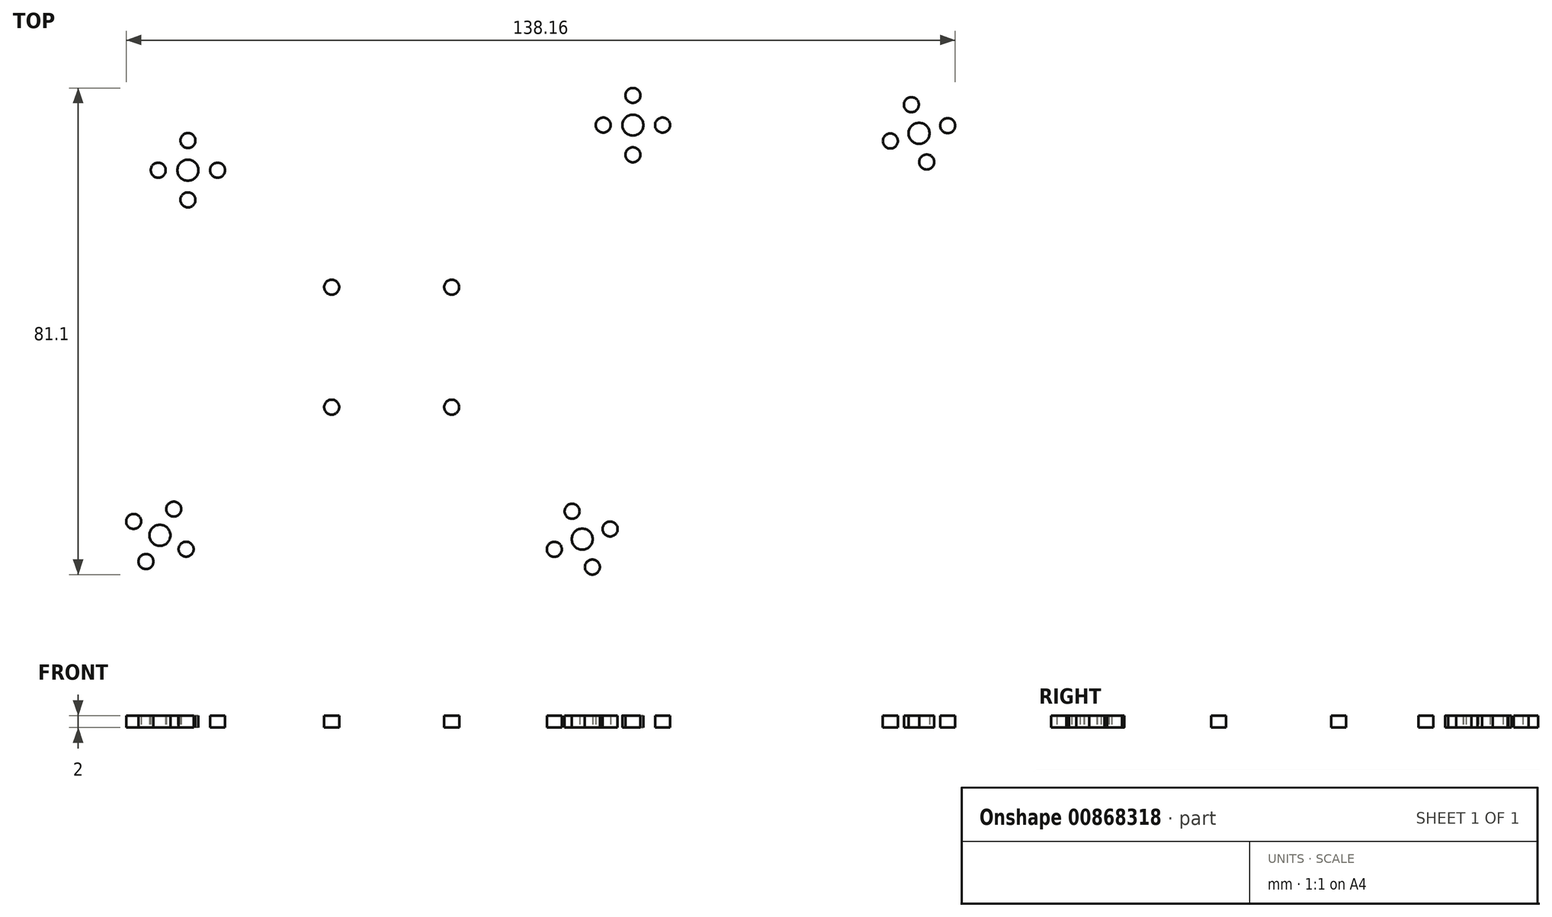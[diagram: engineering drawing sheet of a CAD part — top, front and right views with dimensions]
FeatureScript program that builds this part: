
annotation { "Feature Type Name" : "Feature", "Feature Type Description" : "" }
export const myFeature = defineFeature(function(context is Context, id is Id, definition is map)
    precondition{}
    {
        {
            var Q0;
            Q0=qCreatedBy(makeId("Top.planeOp"),FACE);
            var sketch = newSketch(context, id + "F0", { "sketchPlane" : qUnion([Q0])});
            skLineSegment(sketch, "E0.bottom", {"start": v(10, -2) * mm, "end": v(-10, -2) * mm, "construction": true});
            skLineSegment(sketch, "E0.top", {"start": v(10, 18) * mm, "end": v(-10, 18) * mm, "construction": true});
            skLineSegment(sketch, "E0.left", {"start": v(10, -2) * mm, "end": v(10, 18) * mm, "construction": true});
            skLineSegment(sketch, "E0.right", {"start": v(-10, -2) * mm, "end": v(-10, 0.75) * mm, "construction": true});
            skCircle(sketch, "E1", {"center": v(-10, 18) * mm, "radius": 1.25 * mm});
            skCircle(sketch, "E2.MirrorC", {"center": v(10, 18) * mm, "radius": 1.25 * mm});
            skCircle(sketch, "E3.MirrorC", {"center": v(-10, -2) * mm, "radius": 1.25 * mm});
            skCircle(sketch, "E4.MirrorC", {"center": v(10, -2) * mm, "radius": 1.25 * mm});
            skLineSegment(sketch, "E5", {"start": v(-11.33, 27.1) * mm, "end": v(-11.33, 27.79) * mm});
            skLineSegment(sketch, "E6", {"start": v(-9.22, 27.79) * mm, "end": v(-5.37, 27.79) * mm});
            skLineSegment(sketch, "E7.MirrorCS", {"start": v(9.22, 27.79) * mm, "end": v(5.37, 27.79) * mm});
            skLineSegment(sketch, "E8.MirrorCS", {"start": v(11.33, 27.1) * mm, "end": v(11.33, 27.8) * mm});
            skArc(sketch, "E9.trimOffspring", {"start": v(14.6, 28.49) * mm, "mid": v(14.6, 28.48) * mm, "end": v(14.6, 28.48) * mm});
            skLineSegment(sketch, "E10", {"start": v(-11.33, 27.79) * mm, "end": v(-11.33, 29.47) * mm});
            skLineSegment(sketch, "E11", {"start": v(-11.33, 29.47) * mm, "end": v(-10.32, 29.47) * mm});
            skLineSegment(sketch, "E12", {"start": v(-10.32, 29.47) * mm, "end": v(-9.22, 27.79) * mm});
            skLineSegment(sketch, "E13.MirrorCS", {"start": v(10.32, 29.47) * mm, "end": v(9.22, 27.79) * mm});
            skLineSegment(sketch, "E14.MirrorCS", {"start": v(11.33, 27.8) * mm, "end": v(11.33, 29.47) * mm});
            skLineSegment(sketch, "E15.MirrorCS", {"start": v(11.33, 29.47) * mm, "end": v(10.32, 29.47) * mm});
            skArc(sketch, "E16.filletArc", {"start": v(-12.02, 25.59) * mm, "mid": v(-11.51, 26.27) * mm, "end": v(-11.33, 27.1) * mm});
            skArc(sketch, "E17.filletArc", {"start": v(11.33, 27.1) * mm, "mid": v(11.51, 26.27) * mm, "end": v(12.02, 25.59) * mm});
            skPoint(sketch, "E18.MirrorCS.end.orphan", {"position": v(0, -19.6) * mm});
            skPoint(sketch, "E19.visualSharp", {"position": v(10.43, -7.52) * mm});
            skLineSegment(sketch, "E20", {"start": v(-6.5, -19.41) * mm, "end": v(-6.71, -19.1) * mm});
            skLineSegment(sketch, "E21", {"start": v(6.71, -19.1) * mm, "end": v(6.5, -19.41) * mm});
            skLineSegment(sketch, "E22", {"start": v(-6.5, -19.41) * mm, "end": v(-0.62, -21.35) * mm});
            skLineSegment(sketch, "E23", {"start": v(0.62, -21.35) * mm, "end": v(6.5, -19.41) * mm});
            skPoint(sketch, "E24.visualSharp", {"position": v(0, -21.55) * mm});
            skArc(sketch, "E24.filletArc", {"start": v(-0.62, -21.35) * mm, "mid": v(0, -21.45) * mm, "end": v(0.62, -21.35) * mm});
            skPoint(sketch, "E25.MirrorCS.end.orphan", {"position": v(13.15, 6.8) * mm});
            skArc(sketch, "E26", {"start": v(-4.4, 26.97) * mm, "mid": v(0, 23.32) * mm, "end": v(4.4, 26.97) * mm});
            skPoint(sketch, "E27.visualSharp", {"position": v(-4.47, 27.79) * mm});
            skArc(sketch, "E27.filletArc", {"start": v(-4.4, 26.97) * mm, "mid": v(-4.73, 27.56) * mm, "end": v(-5.37, 27.79) * mm});
            skPoint(sketch, "E28.visualSharp", {"position": v(4.47, 27.79) * mm});
            skArc(sketch, "E28.filletArc", {"start": v(5.37, 27.79) * mm, "mid": v(4.73, 27.56) * mm, "end": v(4.4, 26.97) * mm});
            skPoint(sketch, "E29.MirrorCS.start.orphan", {"position": v(11.6, -8.05) * mm});
            skPoint(sketch, "E30.MirrorCS.end.orphan", {"position": v(11.86, -7.11) * mm});
            skPoint(sketch, "E31.MirrorCS.end.orphan", {"position": v(10.43, -4.56) * mm});
            skPoint(sketch, "E32.visualSharp", {"position": v(-10.43, -4.56) * mm});
            skArc(sketch, "E33.0", {"start": v(-7.26, -1.73) * mm, "mid": v(-7.25, -1.86) * mm, "end": v(-7.25, -2) * mm});
            skLineSegment(sketch, "E34", {"start": v(-10, 0.75) * mm, "end": v(-10, 15.4) * mm});
            skLineSegment(sketch, "E35", {"start": v(-10, 3.97) * mm, "end": v(-10, 0.75) * mm});
            skArc(sketch, "E36.trimOffspring", {"start": v(-11.74, 0.13) * mm, "mid": v(-11.74, 0.13) * mm, "end": v(-11.74, 0.13) * mm});
            skPoint(sketch, "E37.visualSharp", {"position": v(-10.6, -4.68) * mm});
            skLineSegment(sketch, "E38.trimOffspring", {"start": v(-10, 3.97) * mm, "end": v(-10, 18) * mm, "construction": true});
            skPoint(sketch, "E39.MirrorP", {"position": v(11.37, 5.5) * mm});
            skCircle(sketch, "E40", {"center": v(40.25, 44.9) * mm, "radius": 31.75 * mm, "construction": true});
            skPoint(sketch, "E41", {"position": v(0, -21.45) * mm});
            skPoint(sketch, "E42", {"position": v(-10, 8.08) * mm});
            skPoint(sketch, "E43", {"position": v(0, 8.08) * mm});
            skLineSegment(sketch, "E44.bottom", {"start": v(13.5, -4.8) * mm, "end": v(-13.5, -4.8) * mm, "construction": true});
            skLineSegment(sketch, "E44.top", {"start": v(13.5, 20.96) * mm, "end": v(-13.5, 20.96) * mm, "construction": true});
            skLineSegment(sketch, "E44.left", {"start": v(13.5, -4.8) * mm, "end": v(13.5, 20.96) * mm, "construction": true});
            skLineSegment(sketch, "E45", {"start": v(38.9, 36.73) * mm, "end": v(18.3, 11.92) * mm});
            skPoint(sketch, "E46.end.orphan", {"position": v(12.66, 6.92) * mm});
            skPoint(sketch, "E47.visualSharp", {"position": v(11.37, 3.57) * mm});
            skArc(sketch, "E47.filletArc", {"start": v(12.06, 4.4) * mm, "mid": v(11.55, 3.5) * mm, "end": v(11.37, 2.49) * mm});
            skPoint(sketch, "E48.trimOffspring.end.orphan", {"position": v(11.82, -4.06) * mm});
            skPoint(sketch, "E49.MirrorCS.start.orphan", {"position": v(12.42, -6.3) * mm});
            skLineSegment(sketch, "E50", {"start": v(11.37, -4.34) * mm, "end": v(11.37, -5.24) * mm});
            skLineSegment(sketch, "E51", {"start": v(11.67, -5.46) * mm, "end": v(11.37, -5.24) * mm});
            skPoint(sketch, "E52.MirrorCS.end.orphan", {"position": v(11.74, 0.13) * mm});
            skPoint(sketch, "E53.MirrorCS.end.orphan", {"position": v(11.37, 0.9) * mm});
            skArc(sketch, "E54.0", {"start": v(11.37, -4.34) * mm, "mid": v(12.69, -2.36) * mm, "end": v(11.94, -0.1) * mm});
            skLineSegment(sketch, "E55", {"start": v(11.37, 2.49) * mm, "end": v(11.37, 1.29) * mm});
            skPoint(sketch, "E56.visualSharp", {"position": v(11.37, 0.34) * mm});
            skArc(sketch, "E56.filletArc", {"start": v(11.37, 1.29) * mm, "mid": v(11.52, 0.54) * mm, "end": v(11.94, -0.1) * mm});
            skPoint(sketch, "E57.MirrorP", {"position": v(-11.37, 0.9) * mm});
            skArc(sketch, "E58.MirrorCS", {"start": v(-14.6, 28.49) * mm, "mid": v(-14.6, 28.48) * mm, "end": v(-14.6, 28.48) * mm});
            skLineSegment(sketch, "E59.MirrorCS", {"start": v(-32.66, 29.21) * mm, "end": v(-12.06, 4.4) * mm});
            skPoint(sketch, "E60.MirrorP", {"position": v(-11.37, 0.34) * mm});
            skLineSegment(sketch, "E61.MirrorCS", {"start": v(-11.37, 2.49) * mm, "end": v(-11.37, 1.29) * mm});
            skPoint(sketch, "E62.MirrorP", {"position": v(-11.37, 3.57) * mm});
            skPoint(sketch, "E63.MirrorP", {"position": v(-11.37, 5.5) * mm});
            skArc(sketch, "E64.MirrorCS", {"start": v(-12.06, 4.4) * mm, "mid": v(-11.55, 3.5) * mm, "end": v(-11.37, 2.49) * mm});
            skArc(sketch, "E65.MirrorCS", {"start": v(-11.37, 1.29) * mm, "mid": v(-11.52, 0.54) * mm, "end": v(-11.94, -0.1) * mm});
            skArc(sketch, "E66.MirrorCS", {"start": v(-11.37, -4.34) * mm, "mid": v(-12.69, -2.36) * mm, "end": v(-11.94, -0.1) * mm});
            skPoint(sketch, "E67.MirrorP", {"position": v(-11.82, -4.06) * mm});
            skLineSegment(sketch, "E68.MirrorCS", {"start": v(-11.37, -4.34) * mm, "end": v(-11.37, -5.24) * mm});
            skLineSegment(sketch, "E69.MirrorCS", {"start": v(-11.7, -5.41) * mm, "end": v(-11.37, -5.24) * mm});
            skPoint(sketch, "E70.MirrorCS.start.orphan", {"position": v(-11.7, -5.41) * mm});
            skLineSegment(sketch, "E71", {"start": v(-13.5, 20.96) * mm, "end": v(-13.5, -4.8) * mm, "construction": true});
            skArc(sketch, "E72.MirrorCS", {"start": v(-35.15, -16.71) * mm, "mid": v(-34.35, -16.93) * mm, "end": v(-33.53, -16.81) * mm});
            skPoint(sketch, "E73.MirrorP", {"position": v(-31.71, -26.26) * mm});
            skPoint(sketch, "E74.MirrorP", {"position": v(-33.53, -16.81) * mm});
            skPoint(sketch, "E75.MirrorP", {"position": v(-30.85, -26.12) * mm});
            skPoint(sketch, "E76.MirrorP", {"position": v(-34.42, -17.15) * mm});
            skCircle(sketch, "E77.MirrorC", {"center": v(-36.31, -18.99) * mm, "radius": 1.25 * mm});
            skCircle(sketch, "E78.MirrorC", {"center": v(-34.26, -25.67) * mm, "radius": 1.25 * mm});
            skPoint(sketch, "E79.MirrorP", {"position": v(-31.97, -26.3) * mm});
            skCircle(sketch, "E80.MirrorC", {"center": v(-38.63, -23.36) * mm, "radius": 1.75 * mm});
            skCircle(sketch, "E81.MirrorC", {"center": v(-43, -21.04) * mm, "radius": 1.25 * mm});
            skArc(sketch, "E82.MirrorCS", {"start": v(-35.15, -16.71) * mm, "mid": v(-45.82, -25.47) * mm, "end": v(-32.11, -27.07) * mm});
            skCircle(sketch, "E83.MirrorC", {"center": v(-40.94, -27.73) * mm, "radius": 1.25 * mm});
            skArc(sketch, "E84.MirrorCS", {"start": v(-30.7, -26.1) * mm, "mid": v(-31.52, -26.42) * mm, "end": v(-32.11, -27.07) * mm});
            skCircle(sketch, "E85", {"center": v(-38.63, -23.36) * mm, "radius": 31.75 * mm, "construction": true});
            skLineSegment(sketch, "E86", {"start": v(-33.53, -16.81) * mm, "end": v(-16.19, -7.75) * mm});
            skLineSegment(sketch, "E87.MirrorCS", {"start": v(27.6, -16.81) * mm, "end": v(11.67, -5.46) * mm});
            skLineSegment(sketch, "E88.MirrorCS", {"start": v(23.53, -25.62) * mm, "end": v(6.71, -19.1) * mm});
            skArc(sketch, "E89.MirrorCS", {"start": v(23.53, -25.62) * mm, "mid": v(24.3, -26.06) * mm, "end": v(24.8, -26.78) * mm});
            skPoint(sketch, "E90.MirrorP", {"position": v(23.67, -25.66) * mm});
            skArc(sketch, "E91.MirrorCS", {"start": v(29.23, -16.94) * mm, "mid": v(28.4, -17.05) * mm, "end": v(27.6, -16.81) * mm});
            skPoint(sketch, "E92.MirrorP", {"position": v(24.5, -25.92) * mm});
            skCircle(sketch, "E93.MirrorC", {"center": v(30.06, -19.35) * mm, "radius": 1.25 * mm});
            skCircle(sketch, "E94.MirrorC", {"center": v(36.4, -22.3) * mm, "radius": 1.25 * mm});
            skCircle(sketch, "E95.MirrorC", {"center": v(27.1, -25.69) * mm, "radius": 1.25 * mm});
            skPoint(sketch, "E96.MirrorP", {"position": v(27.6, -16.81) * mm});
            skPoint(sketch, "E97.MirrorP", {"position": v(24.76, -26) * mm});
            skCircle(sketch, "E98.MirrorC", {"center": v(33.45, -28.65) * mm, "radius": 1.25 * mm});
            skCircle(sketch, "E99.MirrorC", {"center": v(31.76, -24) * mm, "radius": 1.75 * mm});
            skPoint(sketch, "E100.MirrorP", {"position": v(28.45, -17.27) * mm});
            skArc(sketch, "E101.MirrorCS", {"start": v(29.23, -16.94) * mm, "mid": v(38.6, -27.08) * mm, "end": v(24.8, -26.78) * mm});
            skLineSegment(sketch, "E102", {"start": v(-12.02, 25.59) * mm, "end": v(-25.78, 36.05) * mm});
            skPoint(sketch, "E103.MirrorCS.start.orphan", {"position": v(-12.02, 25.59) * mm});
            skPoint(sketch, "E104.MirrorP", {"position": v(37.37, 35.03) * mm});
            skLineSegment(sketch, "E105", {"start": v(32.02, 43.56) * mm, "end": v(18.26, 33.1) * mm});
            skArc(sketch, "E106.MirrorCS", {"start": v(-26.46, 37.53) * mm, "mid": v(-26.28, 36.72) * mm, "end": v(-25.78, 36.05) * mm});
            skPoint(sketch, "E107.MirrorP", {"position": v(-33.28, 30.02) * mm});
            skPoint(sketch, "E108.MirrorP", {"position": v(-25.78, 36.05) * mm});
            skPoint(sketch, "E109.MirrorP", {"position": v(-32.75, 29.33) * mm});
            skPoint(sketch, "E110.MirrorP", {"position": v(-26.5, 36.68) * mm});
            skCircle(sketch, "E111.MirrorC", {"center": v(-29.01, 37.5) * mm, "radius": 1.25 * mm});
            skCircle(sketch, "E112.MirrorC", {"center": v(-33.96, 32.55) * mm, "radius": 1.25 * mm});
            skPoint(sketch, "E113.MirrorP", {"position": v(-33.44, 30.23) * mm});
            skCircle(sketch, "E114.MirrorC", {"center": v(-33.96, 37.5) * mm, "radius": 1.75 * mm});
            skCircle(sketch, "E115.MirrorC", {"center": v(-33.96, 42.44) * mm, "radius": 1.25 * mm});
            skArc(sketch, "E116.MirrorCS", {"start": v(-26.46, 37.53) * mm, "mid": v(-39.2, 42.86) * mm, "end": v(-34.19, 30) * mm});
            skCircle(sketch, "E117.MirrorC", {"center": v(-38.9, 37.5) * mm, "radius": 1.25 * mm});
            skArc(sketch, "E118.MirrorCS", {"start": v(-32.66, 29.21) * mm, "mid": v(-33.34, 29.77) * mm, "end": v(-34.19, 30) * mm});
            skArc(sketch, "E119.MirrorCS", {"start": v(89.86, 36.4) * mm, "mid": v(89.12, 36.02) * mm, "end": v(88.6, 35.37) * mm});
            skPoint(sketch, "E120.MirrorP", {"position": v(80.84, 41.06) * mm});
            skPoint(sketch, "E121.MirrorP", {"position": v(88.6, 35.37) * mm});
            skPoint(sketch, "E122.MirrorP", {"position": v(80.3, 40.36) * mm});
            skPoint(sketch, "E123.MirrorP", {"position": v(89.03, 36.23) * mm});
            skCircle(sketch, "E124.MirrorC", {"center": v(89.16, 38.86) * mm, "radius": 1.25 * mm});
            skCircle(sketch, "E125.MirrorC", {"center": v(83.1, 42.36) * mm, "radius": 1.25 * mm});
            skPoint(sketch, "E126.MirrorP", {"position": v(81, 41.26) * mm});
            skCircle(sketch, "E127.MirrorC", {"center": v(87.88, 43.64) * mm, "radius": 1.75 * mm});
            skCircle(sketch, "E128.MirrorC", {"center": v(92.66, 44.92) * mm, "radius": 1.25 * mm});
            skArc(sketch, "E129.MirrorCS", {"start": v(89.86, 36.4) * mm, "mid": v(91.71, 50.09) * mm, "end": v(80.58, 41.92) * mm});
            skCircle(sketch, "E130.MirrorC", {"center": v(86.6, 48.42) * mm, "radius": 1.25 * mm});
            skArc(sketch, "E131.MirrorCS", {"start": v(80.22, 40.25) * mm, "mid": v(80.59, 41.04) * mm, "end": v(80.58, 41.92) * mm});
            skArc(sketch, "E132.MirrorCS", {"start": v(32.7, 45.05) * mm, "mid": v(32.52, 44.24) * mm, "end": v(32.02, 43.56) * mm});
            skArc(sketch, "E133.MirrorCS", {"start": v(38.9, 36.73) * mm, "mid": v(39.58, 37.3) * mm, "end": v(40.43, 37.51) * mm});
            skPoint(sketch, "E134.MirrorP", {"position": v(39.52, 37.54) * mm});
            skPoint(sketch, "E135.MirrorP", {"position": v(39, 36.84) * mm});
            skPoint(sketch, "E136.MirrorP", {"position": v(39.68, 37.75) * mm});
            skCircle(sketch, "E137.MirrorC", {"center": v(40.2, 49.95) * mm, "radius": 1.25 * mm});
            skCircle(sketch, "E138.MirrorC", {"center": v(40.2, 45) * mm, "radius": 1.75 * mm});
            skPoint(sketch, "E139.MirrorP", {"position": v(32.74, 44.2) * mm});
            skCircle(sketch, "E140.MirrorC", {"center": v(35.25, 45) * mm, "radius": 1.25 * mm});
            skCircle(sketch, "E141.MirrorC", {"center": v(40.2, 40.06) * mm, "radius": 1.25 * mm});
            skCircle(sketch, "E142.MirrorC", {"center": v(45.14, 45) * mm, "radius": 1.25 * mm});
            skArc(sketch, "E143.MirrorCS", {"start": v(32.7, 45.05) * mm, "mid": v(45.43, 50.38) * mm, "end": v(40.43, 37.51) * mm});
            skLineSegment(sketch, "E144", {"start": v(-16.19, -7.75) * mm, "end": v(-11.7, -5.41) * mm});
            skLineSegment(sketch, "E145", {"start": v(-30.7, -26.1) * mm, "end": v(-6.71, -19.1) * mm});
            skPoint(sketch, "E146.orphan", {"position": v(0, 0.7) * mm});
            skSolve(sketch);
        }
        {
            var Q0;
            Q0 = qSketchRegion(id + "F0", true);
            extrude(context, id + "F1", {"entities" : qUnion([Q0]), "depth" : 2 * mm, "offsetDistance" : 25 * mm});
        }
        {
            var Q0;
            Q0=makeQuery(id+"F1.opExtrude","CAP_FACE",FACE,{"disambiguationData":[OSD([sQuery(id+"F0.wireOp",EDGE,"E1"),sQuery(id+"F0.wireOp",EDGE,"E2.MirrorC"),sQuery(id+"F0.wireOp",EDGE,"E3.MirrorC"),sQuery(id+"F0.wireOp",EDGE,"E4.MirrorC"),sQuery(id+"F0.wireOp",EDGE,"f06bca8e-b852-40d2-a15b-367c443a700f"),sQuery(id+"F0.wireOp",EDGE,"E5"),sQuery(id+"F0.wireOp",EDGE,"E6"),sQuery(id+"F0.wireOp",EDGE,"E7.MirrorCS"),sQuery(id+"F0.wireOp",EDGE,"E8.MirrorCS"),sQuery(id+"F0.wireOp",EDGE,"67ac48d2-fa6a-4aab-9c2c-f520632517a6"),sQuery(id+"F0.wireOp",EDGE,"68e8db3e-4f9a-4987-a184-4165960488de.MirrorCS"),sQuery(id+"F0.wireOp",EDGE,"32d5421f-20f9-4ce5-974c-3a7e300832b9"),sQuery(id+"F0.wireOp",EDGE,"312e11af-75eb-49d6-9b73-eb9da3d24865.MirrorCS"),sQuery(id+"F0.wireOp",EDGE,"6a10c672-6a66-4438-b0d1-d19f12d865f6.trimOffspring"),sQuery(id+"F0.wireOp",EDGE,"E9.trimOffspring"),sQuery(id+"F0.wireOp",EDGE,"E10"),sQuery(id+"F0.wireOp",EDGE,"E11"),sQuery(id+"F0.wireOp",EDGE,"E12"),sQuery(id+"F0.wireOp",EDGE,"E13.MirrorCS"),sQuery(id+"F0.wireOp",EDGE,"E14.MirrorCS"),sQuery(id+"F0.wireOp",EDGE,"E15.MirrorCS"),sQuery(id+"F0.wireOp",EDGE,"2ded7028-2bfa-457d-8319-f162e791f1cb.filletArc"),sQuery(id+"F0.wireOp",EDGE,"35d64ce9-d00c-459c-8b8c-c760b21b0a05.filletArc"),sQuery(id+"F0.wireOp",EDGE,"E16.filletArc"),sQuery(id+"F0.wireOp",EDGE,"E17.filletArc"),sQuery(id+"F0.wireOp",EDGE,"0ccc51ae-7dde-4ee6-8e10-d9e08c1173a2"),sQuery(id+"F0.wireOp",EDGE,"e2719067-e5d4-4f0f-a8d9-f0aa746ee886.filletArc"),sQuery(id+"F0.wireOp",EDGE,"E19.filletArc"),sQuery(id+"F0.wireOp",EDGE,"PLkptYVp-p5mr-Jujz-wegh-2JCMWHGk9esj"),sQuery(id+"F0.wireOp",EDGE,"rTmfKwOO-TQrm-nyj4-MGIQ-Lmup0VidCQIz"),sQuery(id+"F0.wireOp",EDGE,"E20"),sQuery(id+"F0.wireOp",EDGE,"E21"),sQuery(id+"F0.wireOp",EDGE,"ca36907b-8b4a-4238-9ba4-ed585a6c8f63.filletArc"),sQuery(id+"F0.wireOp",EDGE,"1aeadfda-725c-407f-8540-a959c85e1474.filletArc"),sQuery(id+"F0.wireOp",EDGE,"ByN8tmR3-9bsc-2uih-5YOh-iXs6Dsyit2Qq"),sQuery(id+"F0.wireOp",EDGE,"bf7d6005-efa3-4d6a-8cc4-c5f707caf97e.0"),sQuery(id+"F0.wireOp",EDGE,"db0a6af4-1b6a-4ecb-b82f-6a67d63e2e5d.filletArc"),sQuery(id+"F0.wireOp",EDGE,"eb931ecd-5f0a-4963-81b5-68becea4c7b00.MirrorCS"),sQuery(id+"F0.wireOp",EDGE,"f5c9b987-2867-4d04-bdd7-671b2f5165750.MirrorCS"),sQuery(id+"F0.wireOp",EDGE,"b5178bfd-1f67-4089-b302-2dcc733a13b40.MirrorCS"),sQuery(id+"F0.wireOp",EDGE,"ecb31784-4b9f-443f-8ba2-139f7b61dbce0.MirrorCS"),sQuery(id+"F0.wireOp",EDGE,"48715136-edbb-4559-a5c8-281d2b228c3a0.MirrorCS"),sQuery(id+"F0.wireOp",EDGE,"dd57ac0a-628a-4775-9296-c1daed5cee020.MirrorCS"),sQuery(id+"F0.wireOp",EDGE,"u1P6RJIJ-FzjQ-nPCE-wFZj-uXL9XivxlDsU"),sQuery(id+"F0.wireOp",EDGE,"E25.MirrorCS")])],"isStart":false});
            var sketch = newSketch(context, id + "F2", { "sketchPlane" : qUnion([Q0])});
            skPoint(sketch, "E147.middle", {"position": v(-0.17, 15.45) * mm});
            skLineSegment(sketch, "E148.bottom", {"start": v(1.01, -13.9) * mm, "end": v(-1.36, -13.9) * mm});
            skLineSegment(sketch, "E148.top", {"start": v(1.01, 18.38) * mm, "end": v(-1.36, 18.38) * mm});
            skLineSegment(sketch, "E148.left", {"start": v(3.01, -11.9) * mm, "end": v(3.01, 16.38) * mm});
            skLineSegment(sketch, "E148.right", {"start": v(-3.36, -11.9) * mm, "end": v(-3.36, 16.38) * mm});
            skPoint(sketch, "E148.middle", {"position": v(-0.17, 2.24) * mm});
            skPoint(sketch, "E149.visualSharp", {"position": v(-3.36, 18.38) * mm});
            skArc(sketch, "E149.filletArc", {"start": v(-1.36, 18.38) * mm, "mid": v(-2.77, 17.8) * mm, "end": v(-3.36, 16.38) * mm});
            skPoint(sketch, "E150.visualSharp", {"position": v(3.01, 18.38) * mm});
            skArc(sketch, "E150.filletArc", {"start": v(3.01, 16.38) * mm, "mid": v(2.43, 17.8) * mm, "end": v(1.01, 18.38) * mm});
            skPoint(sketch, "E151.visualSharp", {"position": v(3.01, -13.9) * mm});
            skArc(sketch, "E151.filletArc", {"start": v(1.01, -13.9) * mm, "mid": v(2.43, -13.3) * mm, "end": v(3.01, -11.9) * mm});
            skPoint(sketch, "E152.visualSharp", {"position": v(-3.36, -13.9) * mm});
            skArc(sketch, "E152.filletArc", {"start": v(-3.36, -11.9) * mm, "mid": v(-2.77, -13.3) * mm, "end": v(-1.36, -13.9) * mm});
            skPoint(sketch, "E153.end.orphan", {"position": v(-8.31, 4.58) * mm});
            skLineSegment(sketch, "E154", {"start": v(-9.9, 8.83) * mm, "end": v(-9.9, 8.83) * mm});
            skPoint(sketch, "E155.visualSharp", {"position": v(-10.81, 8.83) * mm});
            skArc(sketch, "E155.filletArc", {"start": v(-11.41, 9.52) * mm, "mid": v(-10.73, 9.01) * mm, "end": v(-9.9, 8.83) * mm});
            skPoint(sketch, "E156.MirrorP", {"position": v(10.81, 8.83) * mm});
            skArc(sketch, "E157.MirrorCS", {"start": v(11.41, 9.52) * mm, "mid": v(10.73, 9.01) * mm, "end": v(9.9, 8.83) * mm});
            skLineSegment(sketch, "E158.MirrorCS", {"start": v(9.9, 8.83) * mm, "end": v(9.9, 8.83) * mm});
            skPoint(sketch, "E159.visualSharp", {"position": v(8.9, 8.83) * mm});
            skArc(sketch, "E159.filletArc", {"start": v(8.9, 9.83) * mm, "mid": v(9.19, 9.13) * mm, "end": v(9.9, 8.83) * mm});
            skPoint(sketch, "E160.visualSharp", {"position": v(-8.9, 8.83) * mm});
            skArc(sketch, "E160.filletArc", {"start": v(-9.9, 8.83) * mm, "mid": v(-9.19, 9.13) * mm, "end": v(-8.9, 9.83) * mm});
            skPoint(sketch, "E161.MirrorCS.start.orphan", {"position": v(11.41, 9.52) * mm});
            skPoint(sketch, "E162.MirrorCS.start.orphan", {"position": v(13.73, 22.97) * mm});
            skPoint(sketch, "E163.MirrorCS.end.orphan", {"position": v(9.82, 20.47) * mm});
            skPoint(sketch, "E164.start.orphan", {"position": v(-8.9, 18.78) * mm});
            skArc(sketch, "E165.0", {"start": v(-11.98, 20.32) * mm, "mid": v(-12.85, 16.9) * mm, "end": v(-9.92, 14.95) * mm});
            skLineSegment(sketch, "E166", {"start": v(-8.9, 9.83) * mm, "end": v(-8.9, 13.95) * mm});
            skPoint(sketch, "E167.visualSharp", {"position": v(-10.63, 20.99) * mm});
            skArc(sketch, "E167.filletArc", {"start": v(-11.98, 20.32) * mm, "mid": v(-11.63, 21.15) * mm, "end": v(-12.1, 21.92) * mm});
            skPoint(sketch, "E168.visualSharp", {"position": v(-8.9, 15.16) * mm});
            skArc(sketch, "E168.filletArc", {"start": v(-8.9, 13.95) * mm, "mid": v(-9.2, 14.67) * mm, "end": v(-9.92, 14.95) * mm});
            skLineSegment(sketch, "E169.MirrorCS", {"start": v(8.9, 9.83) * mm, "end": v(8.9, 13.95) * mm});
            skLineSegment(sketch, "E170.MirrorCS", {"start": v(11.41, 9.52) * mm, "end": v(23.32, 23.14) * mm});
            skArc(sketch, "E171.MirrorCS", {"start": v(8.9, 13.95) * mm, "mid": v(9.2, 14.67) * mm, "end": v(9.92, 14.95) * mm});
            skArc(sketch, "E172.MirrorCS", {"start": v(11.98, 20.32) * mm, "mid": v(12.85, 16.9) * mm, "end": v(9.92, 14.95) * mm});
            skArc(sketch, "E173.MirrorCS", {"start": v(11.98, 20.32) * mm, "mid": v(11.63, 21.15) * mm, "end": v(12.1, 21.92) * mm});
            skLineSegment(sketch, "E174.MirrorCS", {"start": v(13.73, 22.97) * mm, "end": v(12.1, 21.92) * mm});
            skSolve(sketch);
        }
        {
            var Q0;
            Q0 = qSketchRegion(id + "F2", true);
            extrude(context, id + "F3", {"entities" : qUnion([Q0]), "operationType" : NewBodyOperationType.REMOVE, "oppositeDirection" : true, "depth" : 2 * mm, "offsetDistance" : 25 * mm});
        }
    });
